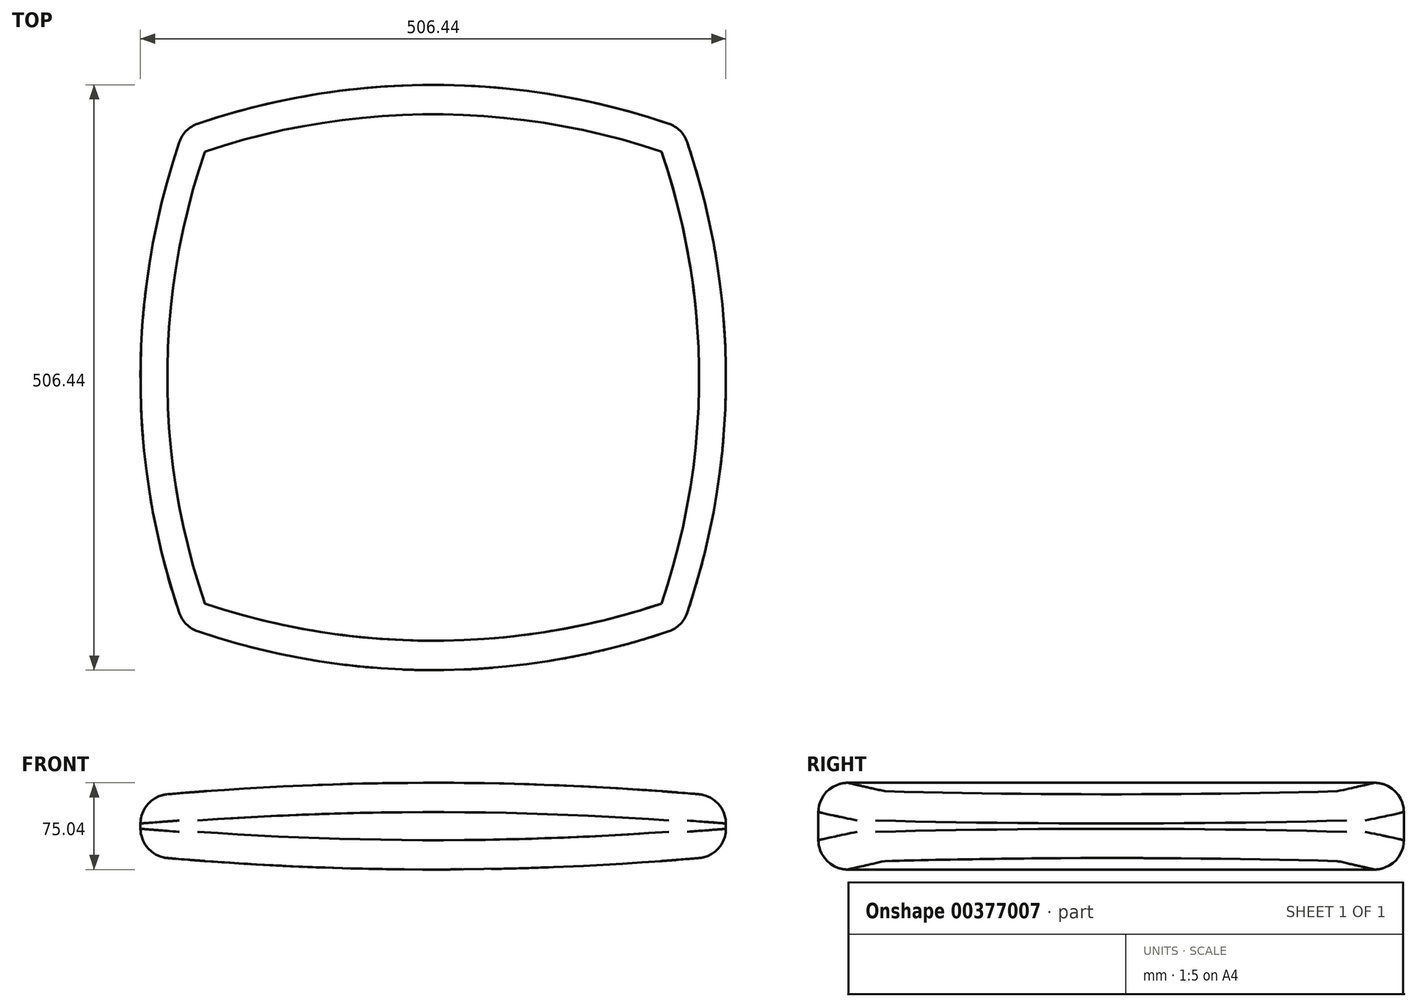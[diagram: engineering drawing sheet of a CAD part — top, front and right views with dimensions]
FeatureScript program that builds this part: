
annotation { "Feature Type Name" : "Feature", "Feature Type Description" : "" }
export const myFeature = defineFeature(function(context is Context, id is Id, definition is map)
    precondition{}
    {
        {
            var Q0;
            Q0=qCreatedBy(makeId("Top.planeOp"),FACE);
            var sketch = newSketch(context, id + "F0", { "sketchPlane" : qUnion([Q0])});
            skLineSegment(sketch, "E0.bottom", {"start": v(254, 254) * mm, "end": v(-254, 254) * mm, "construction": true});
            skLineSegment(sketch, "E0.top", {"start": v(254, -254) * mm, "end": v(-254, -254) * mm, "construction": true});
            skLineSegment(sketch, "E0.left", {"start": v(254, 254) * mm, "end": v(254, -254) * mm, "construction": true});
            skLineSegment(sketch, "E0.right", {"start": v(-254, 254) * mm, "end": v(-254, -254) * mm, "construction": true});
            skPoint(sketch, "E0.middle", {"position": v(0, 0) * mm});
            skLineSegment(sketch, "E1", {"start": v(-254, 254) * mm, "end": v(254, -254) * mm, "construction": true});
            skLineSegment(sketch, "E2", {"start": v(-254, -254) * mm, "end": v(254, 254) * mm, "construction": true});
            skArc(sketch, "E3", {"start": v(-215.53, 215.53) * mm, "mid": v(-253.22, 0) * mm, "end": v(-215.53, -215.53) * mm});
            skArc(sketch, "E4", {"start": v(215.53, 215.53) * mm, "mid": v(0, 253.22) * mm, "end": v(-215.53, 215.53) * mm});
            skArc(sketch, "E5", {"start": v(215.53, -215.53) * mm, "mid": v(253.22, 0) * mm, "end": v(215.53, 215.53) * mm});
            skArc(sketch, "E6", {"start": v(-215.53, -215.53) * mm, "mid": v(0, -253.22) * mm, "end": v(215.53, -215.53) * mm});
            skSolve(sketch);
        }
        {
            var Q0;
            Q0=makeQuery(id+"F0.imprint","IMPRINT",FACE,{"disambiguationData":[TD([[makeQuery(id+"F0.imprint","IMPRINT",EDGE,{"derivedFrom":sQuery(id+"F0.wireOp",EDGE,"E3")}),1.0]])]});
            extrude(context, id + "F1", {"entities" : qUnion([Q0]), "depth" : 76.2 * mm});
        }
        {
            var Q0;
            Q0=qCreatedBy(makeId("Front.planeOp"),FACE);
            var sketch = newSketch(context, id + "F2", { "sketchPlane" : qUnion([Q0])});
            skArc(sketch, "E7", {"start": v(254, 63.5) * mm, "mid": v(0, 75.62) * mm, "end": v(-254, 63.5) * mm});
            skArc(sketch, "E8", {"start": v(-254, 12.7) * mm, "mid": v(0, 0.58) * mm, "end": v(254, 12.7) * mm});
            skLineSegment(sketch, "E9", {"start": v(-254, 12.7) * mm, "end": v(-254, -25.4) * mm});
            skLineSegment(sketch, "E10", {"start": v(-254, -25.4) * mm, "end": v(254, -25.4) * mm});
            skLineSegment(sketch, "E11", {"start": v(254, -25.4) * mm, "end": v(254, 12.7) * mm});
            skLineSegment(sketch, "E12", {"start": v(-254, 63.5) * mm, "end": v(-254, 101.6) * mm});
            skLineSegment(sketch, "E13", {"start": v(-254, 101.6) * mm, "end": v(254, 101.6) * mm});
            skLineSegment(sketch, "E14", {"start": v(254, 101.6) * mm, "end": v(254, 63.5) * mm});
            skSolve(sketch);
        }
        {
            var Q0;
            Q0=makeQuery(id+"F2.imprint","IMPRINT",FACE,{"disambiguationData":[TD([[makeQuery(id+"F2.imprint","IMPRINT",EDGE,{"derivedFrom":sQuery(id+"F2.wireOp",EDGE,"E7")}),-1.0]])]});
            var Q1;
            Q1=makeQuery(id+"F2.imprint","IMPRINT",FACE,{"disambiguationData":[TD([[makeQuery(id+"F2.imprint","IMPRINT",EDGE,{"derivedFrom":sQuery(id+"F2.wireOp",EDGE,"E8")}),-1.0]])]});
            extrude(context, id + "F3", {"entities" : qUnion([Q0, Q1]), "operationType" : NewBodyOperationType.REMOVE, "endBound" : BoundingType.THROUGH_ALL, "oppositeDirection" : true, "depth" : 25.4 * mm, "hasSecondDirection" : true, "secondDirectionBound" : SecondDirectionBoundingType.THROUGH_ALL, "secondDirectionOppositeDirection" : false, "secondDirectionDepth" : 25.4 * mm});
        }
        {
            var Q0;
            Q0=makeQuery(id+"F3.boolean.opBoolean","INTERSECT",EDGE,{"derivedFrom":[makeQuery(id+"F1.opExtrude","SWEPT_FACE",FACE,{"disambiguationData":[OSD([sQuery(id+"F0.wireOp",EDGE,"E5")])]}),makeQuery(id+"F3.opExtrude","SWEPT_FACE",FACE,{"disambiguationData":[OSD([sQuery(id+"F2.wireOp",EDGE,"E7")])]})]});
            var Q1;
            Q1=makeQuery(id+"F3.boolean.opBoolean","COPY",FACE,{"derivedFrom":makeQuery(id+"F3.opExtrude","SWEPT_FACE",FACE,{"disambiguationData":[OSD([sQuery(id+"F2.wireOp",EDGE,"E7")])]})});
            var Q2;
            Q2=makeQuery(id+"F3.boolean.opBoolean","COPY",FACE,{"derivedFrom":makeQuery(id+"F3.opExtrude","SWEPT_FACE",FACE,{"disambiguationData":[OSD([sQuery(id+"F2.wireOp",EDGE,"E8")])]})});
            var Q3;
            Q3=makeQuery(id+"F1.opExtrude","SWEPT_EDGE",EDGE,{"disambiguationData":[OSD([sQuery(id+"F0.wireOp",EDGE,"E5"),sQuery(id+"F0.wireOp",EDGE,"E6")])]});
            var Q4;
            Q4=makeQuery(id+"F1.opExtrude","SWEPT_EDGE",EDGE,{"disambiguationData":[OSD([sQuery(id+"F0.wireOp",EDGE,"E4"),sQuery(id+"F0.wireOp",EDGE,"E5")])]});
            var Q5;
            Q5=makeQuery(id+"F1.opExtrude","SWEPT_EDGE",EDGE,{"disambiguationData":[OSD([sQuery(id+"F0.wireOp",EDGE,"E3"),sQuery(id+"F0.wireOp",EDGE,"E4")])]});
            var Q6;
            Q6=makeQuery(id+"F1.opExtrude","SWEPT_EDGE",EDGE,{"disambiguationData":[OSD([sQuery(id+"F0.wireOp",EDGE,"E3"),sQuery(id+"F0.wireOp",EDGE,"E6")])]});
            fillet(context, id + "F4", {"entities" : qUnion([Q0, Q1, Q2, Q3, Q4, Q5, Q6]), "radius" : 25.4 * mm, "tangentPropagation" : true, "allowEdgeOverflow" : false});
        }
    });
